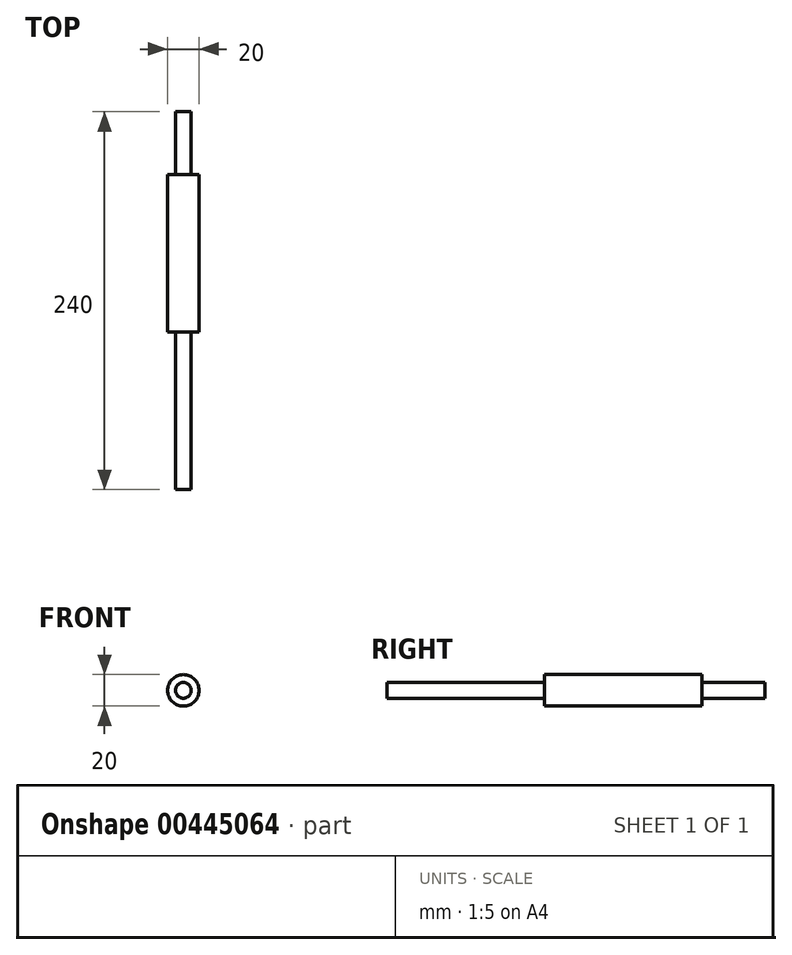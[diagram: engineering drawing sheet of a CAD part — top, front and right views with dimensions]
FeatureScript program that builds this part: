
annotation { "Feature Type Name" : "Feature", "Feature Type Description" : "" }
export const myFeature = defineFeature(function(context is Context, id is Id, definition is map)
    precondition{}
    {
        {
            var Q0;
            Q0=qCreatedBy(makeId("Front.planeOp"),FACE);
            var sketch = newSketch(context, id + "F0", { "sketchPlane" : qUnion([Q0])});
            skCircle(sketch, "E0", {"center": v(0, 0) * mm, "radius": 5 * mm});
            skSolve(sketch);
        }
        {
            var Q0;
            Q0=makeQuery(id+"F0.imprint","IMPRINT",FACE,{"disambiguationData":[TD([[makeQuery(id+"F0.imprint","IMPRINT",EDGE,{"derivedFrom":sQuery(id+"F0.wireOp",EDGE,"E0")}),1.0]])]});
            extrude(context, id + "F1", {"entities" : qUnion([Q0]), "depth" : 40 * mm});
        }
        {
            var Q0;
            Q0=makeQuery(id+"F1.opExtrude","CAP_FACE",FACE,{"disambiguationData":[OSD([sQuery(id+"F0.wireOp",EDGE,"E0")])],"isStart":false});
            var sketch = newSketch(context, id + "F2", { "sketchPlane" : qUnion([Q0])});
            skSolve(sketch);
        }
        {
            var Q0;
            Q0=makeQuery(id+"F2.imprint","IMPRINT",FACE,{"disambiguationData":[TD([[makeQuery(id+"F2.imprint","IMPRINT",EDGE,{"derivedFrom":makeQuery(id+"F1.opExtrude","CAP_EDGE",EDGE,{"disambiguationData":[OSD([sQuery(id+"F0.wireOp",EDGE,"E0")])],"isStart":false})}),1.0]])]});
            var sketch = newSketch(context, id + "F3", { "sketchPlane" : qUnion([Q0])});
            skCircle(sketch, "E1", {"center": v(0, 0) * mm, "radius": 10 * mm});
            skSolve(sketch);
        }
        {
            var Q0;
            Q0=makeQuery(id+"F2.imprint","IMPRINT",FACE,{"disambiguationData":[TD([[makeQuery(id+"F2.imprint","IMPRINT",EDGE,{"derivedFrom":makeQuery(id+"F1.opExtrude","CAP_EDGE",EDGE,{"disambiguationData":[OSD([sQuery(id+"F0.wireOp",EDGE,"E0")])],"isStart":false})}),1.0]])]});
            extrude(context, id + "F4", {"entities" : qUnion([Q0]), "operationType" : NewBodyOperationType.ADD, "depth" : 200 * mm});
        }
        {
            var Q0;
            Q0=makeQuery(id+"F3.imprint","IMPRINT",FACE,{"disambiguationData":[TD([[makeQuery(id+"F3.imprint","IMPRINT",EDGE,{"derivedFrom":sQuery(id+"F3.wireOp",EDGE,"E1")}),1.0]])]});
            extrude(context, id + "F5", {"entities" : qUnion([Q0]), "operationType" : NewBodyOperationType.ADD, "depth" : 100 * mm});
        }
    });
